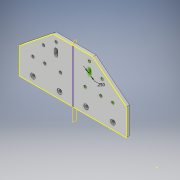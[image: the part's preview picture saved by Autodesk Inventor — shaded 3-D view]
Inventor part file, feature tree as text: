
AUTODESK INVENTOR PART (.ipt)
format: ipt  version: 2017 (Build 210142000, 142)  size: 162,816 bytes
history: native  units: in
note: dims shown in document units (in); Inventor stores cm internally (conversion verified against a paired STEP export)
features: sketch x4, extrude x2, hole x2, projected_geometry x2, pattern_linear x1, plane x1, mirror x1
ambient origin geometry x8: Origin, YZ Plane, XZ Plane, XY Plane, X Axis, Y Axis, Z Axis, Center Point
bodies: Solid1 (feature_tree)
feature tree (13):
  extrude  "Extrusion1"  Depth=8.0in
  hole  "Hole1"  [1 undecoded]
  pattern_linear  "Rectangular Pattern1"  Spacing1=0.25in  [1 undecoded]
  sketch  "Sketch3"  dims[d4=3.0in]
  hole  "Hole2"  [1 undecoded]
  extrude  "Extrusion2"  Depth=0.25in
  sketch  "Sketch4"  dims[d5=2.5in d6=0.25in d7=0.0in d8=0.5in d9=1.0in d10=0.196in d11=0.5in d12=0.375in d13=0.05in d14=0.5635in d15=0.75in d16=0.8108in d17=1.5748in d19=2.0in d20=0.25in d21=0.196in d22=0.5in d23=0.375in d24=0.25in d25=0.5635in d26=0.75in d27=0.8108in d28=1.0in d29=0.0in d30=0.0in]
  plane  "Work Plane1"
  mirror  "Mirror1"
  sketch  "Sketch1"  dims[d0=8.0in d1=2.0in]
  sketch  "Sketch2"  dims[d2=2.0in d3=4.0in]
  projected_geometry  "Projected Loop1"
  projected_geometry  "Projected Loop2"
note: 3 required parameter values undecoded (feature->parameter linkage not recoverable at this tier; creation-order binding heuristic only, values carry confidence <= 0.55)
